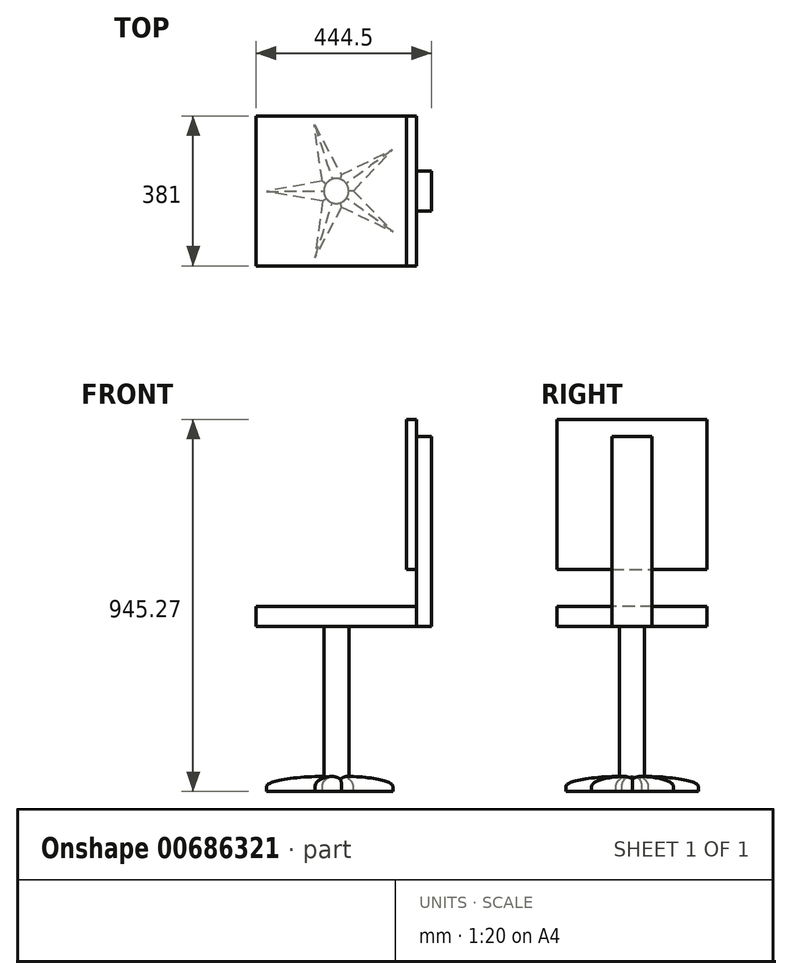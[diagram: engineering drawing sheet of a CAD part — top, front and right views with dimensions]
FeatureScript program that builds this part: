
annotation { "Feature Type Name" : "Feature", "Feature Type Description" : "" }
export const myFeature = defineFeature(function(context is Context, id is Id, definition is map)
    precondition{}
    {
        {
            var Q0;
            Q0=qCreatedBy(makeId("Top.planeOp"),FACE);
            var sketch = newSketch(context, id + "F0", { "sketchPlane" : qUnion([Q0])});
            skLineSegment(sketch, "E0.bottom", {"start": v(-203.2, 190.5) * mm, "end": v(203.2, 190.5) * mm});
            skLineSegment(sketch, "E0.top", {"start": v(-203.2, -190.5) * mm, "end": v(203.2, -190.5) * mm});
            skLineSegment(sketch, "E0.left", {"start": v(-203.2, 190.5) * mm, "end": v(-203.2, -190.5) * mm});
            skLineSegment(sketch, "E0.right", {"start": v(203.2, 190.5) * mm, "end": v(203.2, -190.5) * mm});
            skPoint(sketch, "E0.middle", {"position": v(0, 0) * mm});
            skSolve(sketch);
        }
        {
            var Q0;
            Q0=makeQuery(id+"F0.imprint","IMPRINT",FACE,{"disambiguationData":[TD([[makeQuery(id+"F0.imprint","IMPRINT",EDGE,{"derivedFrom":sQuery(id+"F0.wireOp",EDGE,"E0.bottom")}),-1.0]])]});
            extrude(context, id + "F1", {"entities" : qUnion([Q0]), "depth" : 50.8 * mm, "offsetDistance" : 25.4 * mm});
        }
        {
            var Q0;
            Q0=makeQuery(id+"F1.opExtrude","SWEPT_FACE",FACE,{"disambiguationData":[OSD([sQuery(id+"F0.wireOp",EDGE,"E0.right")])]});
            var sketch = newSketch(context, id + "F2", { "sketchPlane" : qUnion([Q0])});
            skLineSegment(sketch, "E1.bottom", {"start": v(50.8, 0) * mm, "end": v(-50.8, 0) * mm});
            skLineSegment(sketch, "E1.top", {"start": v(50.8, 482.6) * mm, "end": v(-50.8, 482.6) * mm});
            skLineSegment(sketch, "E1.left", {"start": v(50.8, 0) * mm, "end": v(50.8, 482.6) * mm});
            skLineSegment(sketch, "E1.right", {"start": v(-50.8, 0) * mm, "end": v(-50.8, 482.6) * mm});
            skSolve(sketch);
        }
        {
            var Q0;
            {var subQ0=sQuery(id+"F2.wireOp",EDGE,"E1.top");Q0=makeQuery(id+"F2.imprint","IMPRINT",FACE,{"disambiguationData":[TD([[makeQuery(id+"F2.imprint","IMPRINT",EDGE,{"derivedFrom":subQ0}),1.0]])]});}
            var Q1;
            {var subQ0=sQuery(id+"F2.wireOp",EDGE,"E1.bottom");Q1=makeQuery(id+"F2.imprint","IMPRINT",FACE,{"disambiguationData":[TD([[makeQuery(id+"F2.imprint","IMPRINT",EDGE,{"derivedFrom":subQ0}),-1.0]])]});}
            extrude(context, id + "F3", {"entities" : qUnion([Q0, Q1]), "operationType" : NewBodyOperationType.ADD, "depth" : 38.1 * mm, "offsetDistance" : 25.4 * mm});
        }
        {
            var Q0;
            Q0=makeQuery(id+"F3.opExtrude","CAP_FACE",FACE,{"disambiguationData":[OSD([sQuery(id+"F2.wireOp",EDGE,"E1.bottom"),sQuery(id+"F2.wireOp",EDGE,"E1.top"),sQuery(id+"F2.wireOp",EDGE,"E1.left"),sQuery(id+"F2.wireOp",EDGE,"E1.right")])],"isStart":true});
            var sketch = newSketch(context, id + "F4", { "sketchPlane" : qUnion([Q0])});
            skLineSegment(sketch, "E2.bottom", {"start": v(190.5, 526.17) * mm, "end": v(-190.5, 526.17) * mm});
            skLineSegment(sketch, "E2.top", {"start": v(190.5, 145.17) * mm, "end": v(-190.5, 145.17) * mm});
            skLineSegment(sketch, "E2.left", {"start": v(190.5, 526.17) * mm, "end": v(190.5, 145.17) * mm});
            skLineSegment(sketch, "E2.right", {"start": v(-190.5, 526.17) * mm, "end": v(-190.5, 145.17) * mm});
            skPoint(sketch, "E2.middle", {"position": v(0, 335.67) * mm});
            skSolve(sketch);
        }
        {
            var Q0;
            Q0=makeQuery(id+"F4.imprint","IMPRINT",FACE,{"disambiguationData":[TD([[makeQuery(id+"F4.imprint","IMPRINT",EDGE,{"derivedFrom":sQuery(id+"F4.wireOp",EDGE,"E2.bottom")}),1.0]])]});
            var Q1;
            {var subQ3=sQuery(id+"F2.wireOp",EDGE,"E1.top");var subQ9=makeQuery(id+"F3.opExtrude","CAP_EDGE",EDGE,{"disambiguationData":[OSD([subQ3])],"isStart":true});Q1=makeQuery(id+"F4.imprint","IMPRINT",FACE,{"disambiguationData":[TD([[makeQuery(id+"F4.imprint","IMPRINT",EDGE,{"derivedFrom":subQ9}),-1.0]])]});}
            extrude(context, id + "F5", {"entities" : qUnion([Q0, Q1]), "operationType" : NewBodyOperationType.ADD, "depth" : 25.4 * mm, "offsetDistance" : 25.4 * mm});
        }
        {
            var Q0;
            Q0=makeQuery(id+"F3.boolean.opBoolean","MERGE",FACE,{"derivedFrom":[makeQuery(id+"F1.opExtrude","CAP_FACE",FACE,{"disambiguationData":[OSD([sQuery(id+"F0.wireOp",EDGE,"E0.bottom"),sQuery(id+"F0.wireOp",EDGE,"E0.top"),sQuery(id+"F0.wireOp",EDGE,"E0.left"),sQuery(id+"F0.wireOp",EDGE,"E0.right")])],"isStart":true}),makeQuery(id+"F3.opExtrude","SWEPT_FACE",FACE,{"disambiguationData":[OSD([sQuery(id+"F2.wireOp",EDGE,"E1.bottom")])]})]});
            var sketch = newSketch(context, id + "F6", { "sketchPlane" : qUnion([Q0])});
            skCircle(sketch, "E3", {"center": v(0, 0) * mm, "radius": 31.75 * mm});
            skSolve(sketch);
        }
        {
            var Q0;
            Q0=makeQuery(id+"F6.imprint","IMPRINT",FACE,{"disambiguationData":[TD([[makeQuery(id+"F6.imprint","IMPRINT",EDGE,{"derivedFrom":sQuery(id+"F6.wireOp",EDGE,"E3")}),1.0]])]});
            extrude(context, id + "F7", {"entities" : qUnion([Q0]), "operationType" : NewBodyOperationType.ADD, "depth" : 381 * mm, "offsetDistance" : 25.4 * mm});
        }
        {
            var Q0;
            Q0=makeQuery(id+"F7.opExtrude","CAP_FACE",FACE,{"disambiguationData":[OSD([sQuery(id+"F6.wireOp",EDGE,"E3")])],"isStart":false});
            var sketch = newSketch(context, id + "F8", { "sketchPlane" : qUnion([Q0])});
            skCircle(sketch, "E4.cCircle", {"center": v(0, 0) * mm, "radius": 143.3 * mm, "construction": true});
            skLineSegment(sketch, "E4.0", {"start": v(-177.13, 1.02) * mm, "end": v(-53.76, 168.77) * mm});
            skLineSegment(sketch, "E4.1", {"start": v(-53.76, 168.77) * mm, "end": v(143.9, 103.29) * mm});
            skLineSegment(sketch, "E4.2", {"start": v(143.9, 103.29) * mm, "end": v(142.7, -104.94) * mm});
            skLineSegment(sketch, "E4.3", {"start": v(142.7, -104.94) * mm, "end": v(-55.7, -168.14) * mm});
            skLineSegment(sketch, "E4.4", {"start": v(-55.7, -168.14) * mm, "end": v(-177.13, 1.02) * mm});
            skPoint(sketch, "E4.0.midPoint", {"position": v(-115.44, 84.9) * mm});
            skPoint(sketch, "E5.orphan", {"position": v(35.41, 1.02) * mm});
            skCircle(sketch, "E6.cCircle", {"center": v(0, 0) * mm, "radius": 31.75 * mm, "construction": true});
            skLineSegment(sketch, "E6.0", {"start": v(-31.73, 1.02) * mm, "end": v(-8.84, 30.5) * mm});
            skLineSegment(sketch, "E6.1", {"start": v(-8.84, 30.5) * mm, "end": v(26.27, 17.83) * mm});
            skLineSegment(sketch, "E6.2", {"start": v(26.27, 17.83) * mm, "end": v(25.07, -19.48) * mm});
            skLineSegment(sketch, "E6.3", {"start": v(25.07, -19.48) * mm, "end": v(-10.78, -29.86) * mm});
            skLineSegment(sketch, "E6.4", {"start": v(-10.78, -29.86) * mm, "end": v(-31.73, 1.02) * mm});
            skPoint(sketch, "E7.start.orphan", {"position": v(0, -31.75) * mm});
            skLineSegment(sketch, "E8", {"start": v(25.07, -19.48) * mm, "end": v(143.9, 103.29) * mm});
            skLineSegment(sketch, "E9", {"start": v(-8.84, 30.5) * mm, "end": v(143.9, 103.29) * mm});
            skLineSegment(sketch, "E10", {"start": v(26.27, 17.83) * mm, "end": v(-53.76, 168.77) * mm});
            skLineSegment(sketch, "E11", {"start": v(-31.73, 1.02) * mm, "end": v(-53.76, 168.77) * mm});
            skLineSegment(sketch, "E12", {"start": v(-8.84, 30.5) * mm, "end": v(-177.13, 1.02) * mm});
            skLineSegment(sketch, "E13", {"start": v(-10.78, -29.86) * mm, "end": v(-177.13, 1.02) * mm});
            skLineSegment(sketch, "E14", {"start": v(-31.73, 1.02) * mm, "end": v(-55.7, -168.14) * mm});
            skLineSegment(sketch, "E15", {"start": v(-55.7, -168.14) * mm, "end": v(25.07, -19.48) * mm});
            skLineSegment(sketch, "E16", {"start": v(-10.78, -29.86) * mm, "end": v(142.7, -104.94) * mm});
            skLineSegment(sketch, "E17", {"start": v(26.27, 17.83) * mm, "end": v(142.7, -104.94) * mm});
            skSolve(sketch);
        }
        {
            var Q0;
            Q0=makeQuery(id+"F8.imprint","IMPRINT",FACE,{"disambiguationData":[TD([[makeQuery(id+"F8.imprint","IMPRINT",EDGE,{"derivedFrom":sQuery(id+"F8.wireOp",EDGE,"E6.0")}),-1.0]])]});
            var Q1;
            {var subQ0=sQuery(id+"F8.wireOp",EDGE,"E6.4");Q1=makeQuery(id+"F8.imprint","IMPRINT",FACE,{"disambiguationData":[TD([[makeQuery(id+"F8.imprint","IMPRINT",EDGE,{"derivedFrom":subQ0}),1.0]])]});}
            var Q2;
            {var subQ0=sQuery(id+"F8.wireOp",EDGE,"E6.0");Q2=makeQuery(id+"F8.imprint","IMPRINT",FACE,{"disambiguationData":[TD([[makeQuery(id+"F8.imprint","IMPRINT",EDGE,{"derivedFrom":subQ0}),1.0]])]});}
            var Q3;
            {var subQ0=sQuery(id+"F8.wireOp",EDGE,"E6.1");Q3=makeQuery(id+"F8.imprint","IMPRINT",FACE,{"disambiguationData":[TD([[makeQuery(id+"F8.imprint","IMPRINT",EDGE,{"derivedFrom":subQ0}),1.0]])]});}
            var Q4;
            {var subQ0=sQuery(id+"F8.wireOp",EDGE,"E6.2");Q4=makeQuery(id+"F8.imprint","IMPRINT",FACE,{"disambiguationData":[TD([[makeQuery(id+"F8.imprint","IMPRINT",EDGE,{"derivedFrom":subQ0}),1.0]])]});}
            var Q5;
            {var subQ0=sQuery(id+"F8.wireOp",EDGE,"E6.3");Q5=makeQuery(id+"F8.imprint","IMPRINT",FACE,{"disambiguationData":[TD([[makeQuery(id+"F8.imprint","IMPRINT",EDGE,{"derivedFrom":subQ0}),1.0]])]});}
            var Q6;
            {var subQ0=sQuery(id+"F8.wireOp",EDGE,"E15");var subQ4=sQuery(id+"F8.wireOp",EDGE,"E16");var subQ5=makeQuery(id+"F8.imprint","INTERSECT",VERTEX,{"derivedFrom":[subQ0,subQ4]});Q6=makeQuery(id+"F8.imprint","IMPRINT",FACE,{"disambiguationData":[TD([[makeQuery(id+"F8.imprint","IMPRINT",EDGE,{"disambiguationData":[TD([[subQ5,-1.0]])],"derivedFrom":subQ0}),1.0]])]});}
            var Q7;
            {var subQ0=sQuery(id+"F8.wireOp",EDGE,"E13");var subQ4=sQuery(id+"F8.wireOp",EDGE,"E14");var subQ5=makeQuery(id+"F8.imprint","INTERSECT",VERTEX,{"derivedFrom":[subQ0,subQ4]});Q7=makeQuery(id+"F8.imprint","IMPRINT",FACE,{"disambiguationData":[TD([[makeQuery(id+"F8.imprint","IMPRINT",EDGE,{"disambiguationData":[TD([[subQ5,1.0]])],"derivedFrom":subQ0}),-1.0]])]});}
            var Q8;
            {var subQ0=sQuery(id+"F8.wireOp",EDGE,"E9");var subQ4=sQuery(id+"F8.wireOp",EDGE,"E10");var subQ5=makeQuery(id+"F8.imprint","INTERSECT",VERTEX,{"derivedFrom":[subQ0,subQ4]});Q8=makeQuery(id+"F8.imprint","IMPRINT",FACE,{"disambiguationData":[TD([[makeQuery(id+"F8.imprint","IMPRINT",EDGE,{"disambiguationData":[TD([[subQ5,1.0]])],"derivedFrom":subQ0}),-1.0]])]});}
            var Q9;
            {var subQ0=sQuery(id+"F8.wireOp",EDGE,"E8");var subQ4=sQuery(id+"F8.wireOp",EDGE,"E17");var subQ5=makeQuery(id+"F8.imprint","INTERSECT",VERTEX,{"derivedFrom":[subQ0,subQ4]});Q9=makeQuery(id+"F8.imprint","IMPRINT",FACE,{"disambiguationData":[TD([[makeQuery(id+"F8.imprint","IMPRINT",EDGE,{"disambiguationData":[TD([[subQ5,1.0]])],"derivedFrom":subQ0}),1.0]])]});}
            var Q10;
            {var subQ0=sQuery(id+"F8.wireOp",EDGE,"E11");var subQ4=sQuery(id+"F8.wireOp",EDGE,"E12");var subQ5=makeQuery(id+"F8.imprint","INTERSECT",VERTEX,{"derivedFrom":[subQ0,subQ4]});Q10=makeQuery(id+"F8.imprint","IMPRINT",FACE,{"disambiguationData":[TD([[makeQuery(id+"F8.imprint","IMPRINT",EDGE,{"disambiguationData":[TD([[subQ5,1.0]])],"derivedFrom":subQ0}),-1.0]])]});}
            var Q11;
            {var subQ1=sQuery(id+"F8.wireOp",EDGE,"E11");var subQ3=sQuery(id+"F8.wireOp",EDGE,"E12");var subQ4=makeQuery(id+"F8.imprint","INTERSECT",VERTEX,{"derivedFrom":[subQ1,subQ3]});Q11=makeQuery(id+"F8.imprint","IMPRINT",FACE,{"disambiguationData":[TD([[makeQuery(id+"F8.imprint","IMPRINT",EDGE,{"disambiguationData":[TD([[subQ4,-1.0]])],"derivedFrom":subQ3}),1.0]])]});}
            var Q12;
            {var subQ1=sQuery(id+"F8.wireOp",EDGE,"E13");var subQ3=sQuery(id+"F8.wireOp",EDGE,"E14");var subQ4=makeQuery(id+"F8.imprint","INTERSECT",VERTEX,{"derivedFrom":[subQ1,subQ3]});Q12=makeQuery(id+"F8.imprint","IMPRINT",FACE,{"disambiguationData":[TD([[makeQuery(id+"F8.imprint","IMPRINT",EDGE,{"disambiguationData":[TD([[subQ4,-1.0]])],"derivedFrom":subQ3}),1.0]])]});}
            var Q13;
            {var subQ1=sQuery(id+"F8.wireOp",EDGE,"E9");var subQ3=sQuery(id+"F8.wireOp",EDGE,"E10");var subQ4=makeQuery(id+"F8.imprint","INTERSECT",VERTEX,{"derivedFrom":[subQ1,subQ3]});Q13=makeQuery(id+"F8.imprint","IMPRINT",FACE,{"disambiguationData":[TD([[makeQuery(id+"F8.imprint","IMPRINT",EDGE,{"disambiguationData":[TD([[subQ4,-1.0]])],"derivedFrom":subQ3}),1.0]])]});}
            var Q14;
            {var subQ1=sQuery(id+"F8.wireOp",EDGE,"E8");var subQ3=sQuery(id+"F8.wireOp",EDGE,"E17");var subQ4=makeQuery(id+"F8.imprint","INTERSECT",VERTEX,{"derivedFrom":[subQ1,subQ3]});Q14=makeQuery(id+"F8.imprint","IMPRINT",FACE,{"disambiguationData":[TD([[makeQuery(id+"F8.imprint","IMPRINT",EDGE,{"disambiguationData":[TD([[subQ4,-1.0]])],"derivedFrom":subQ1}),1.0]])]});}
            var Q15;
            {var subQ0=sQuery(id+"F8.wireOp",EDGE,"E15");var subQ5=sQuery(id+"F8.wireOp",EDGE,"E16");var subQ6=makeQuery(id+"F8.imprint","INTERSECT",VERTEX,{"derivedFrom":[subQ0,subQ5]});Q15=makeQuery(id+"F8.imprint","IMPRINT",FACE,{"disambiguationData":[TD([[makeQuery(id+"F8.imprint","IMPRINT",EDGE,{"disambiguationData":[TD([[subQ6,-1.0]])],"derivedFrom":subQ5}),1.0]])]});}
            extrude(context, id + "F9", {"entities" : qUnion([Q0, Q1, Q2, Q3, Q4, Q5, Q6, Q7, Q8, Q9, Q10, Q11, Q12, Q13, Q14, Q15]), "operationType" : NewBodyOperationType.ADD, "depth" : 38.1 * mm, "offsetDistance" : 25.4 * mm});
        }
        {
            var Q0;
            Q0=makeQuery(id+"F9.opExtrude","CAP_EDGE",EDGE,{"disambiguationData":[OSD([sQuery(id+"F8.wireOp",EDGE,"E13")])],"isStart":true});
            var Q1;
            Q1=makeQuery(id+"F9.opExtrude","CAP_EDGE",EDGE,{"disambiguationData":[OSD([sQuery(id+"F8.wireOp",EDGE,"E12")])],"isStart":true});
            var Q2;
            Q2=makeQuery(id+"F9.opExtrude","CAP_EDGE",EDGE,{"disambiguationData":[OSD([sQuery(id+"F8.wireOp",EDGE,"E11")])],"isStart":true});
            var Q3;
            Q3=makeQuery(id+"F9.opExtrude","CAP_EDGE",EDGE,{"disambiguationData":[OSD([sQuery(id+"F8.wireOp",EDGE,"E10")])],"isStart":true});
            var Q4;
            Q4=makeQuery(id+"F9.opExtrude","CAP_EDGE",EDGE,{"disambiguationData":[OSD([sQuery(id+"F8.wireOp",EDGE,"E9")])],"isStart":true});
            var Q5;
            Q5=makeQuery(id+"F9.opExtrude","CAP_EDGE",EDGE,{"disambiguationData":[OSD([sQuery(id+"F8.wireOp",EDGE,"E14")])],"isStart":true});
            var Q6;
            Q6=makeQuery(id+"F9.opExtrude","CAP_EDGE",EDGE,{"disambiguationData":[OSD([sQuery(id+"F8.wireOp",EDGE,"E15")])],"isStart":true});
            var Q7;
            Q7=makeQuery(id+"F9.opExtrude","CAP_EDGE",EDGE,{"disambiguationData":[OSD([sQuery(id+"F8.wireOp",EDGE,"E16")])],"isStart":true});
            var Q8;
            Q8=makeQuery(id+"F9.opExtrude","CAP_EDGE",EDGE,{"disambiguationData":[OSD([sQuery(id+"F8.wireOp",EDGE,"E8")])],"isStart":true});
            var Q9;
            Q9=makeQuery(id+"F9.opExtrude","CAP_EDGE",EDGE,{"disambiguationData":[OSD([sQuery(id+"F8.wireOp",EDGE,"E17")])],"isStart":true});
            fillet(context, id + "F10", {"entities" : qUnion([Q0, Q1, Q2, Q3, Q4, Q5, Q6, Q7, Q8, Q9]), "radius" : 25.4 * mm, "tangentPropagation" : true, "allowEdgeOverflow" : false});
        }
    });
